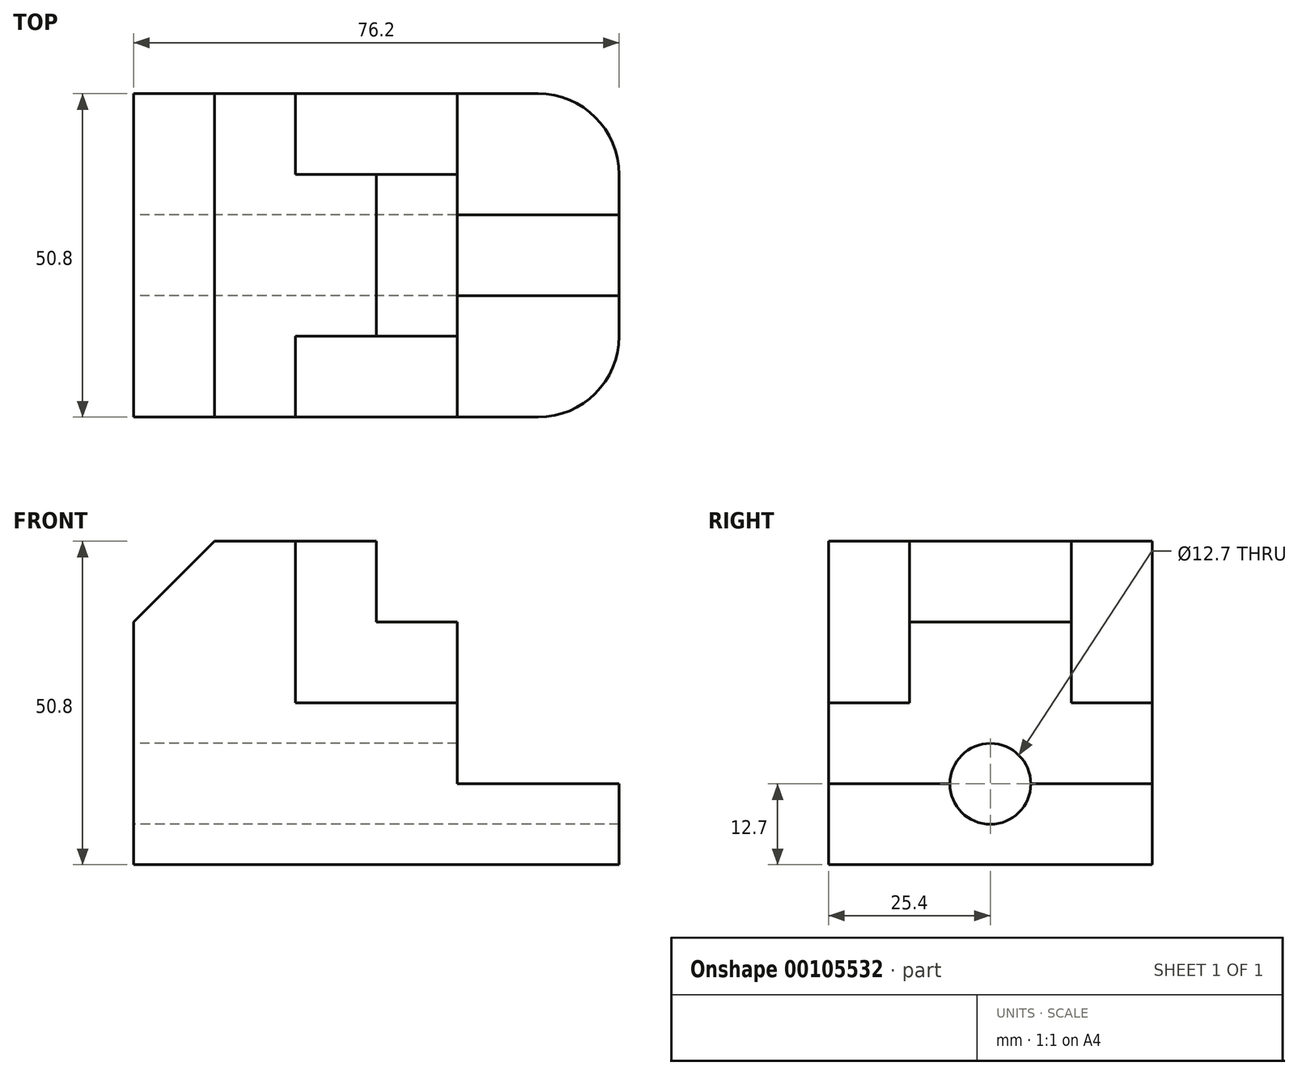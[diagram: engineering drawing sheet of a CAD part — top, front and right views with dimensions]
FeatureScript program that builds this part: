
annotation { "Feature Type Name" : "Feature", "Feature Type Description" : "" }
export const myFeature = defineFeature(function(context is Context, id is Id, definition is map)
    precondition{}
    {
        {
            var Q0;
            Q0=qCreatedBy(makeId("Front.planeOp"),FACE);
            var sketch = newSketch(context, id + "F0", { "sketchPlane" : qUnion([Q0])});
            skLineSegment(sketch, "E0", {"start": v(0, 0) * mm, "end": v(76.2, 0) * mm});
            skLineSegment(sketch, "E1", {"start": v(76.2, 0) * mm, "end": v(76.2, 12.7) * mm});
            skLineSegment(sketch, "E2", {"start": v(76.2, 12.7) * mm, "end": v(50.8, 12.7) * mm});
            skLineSegment(sketch, "E3", {"start": v(50.8, 12.7) * mm, "end": v(50.8, 25.4) * mm});
            skLineSegment(sketch, "E4", {"start": v(50.8, 25.4) * mm, "end": v(25.4, 25.4) * mm});
            skLineSegment(sketch, "E5", {"start": v(25.4, 25.4) * mm, "end": v(25.4, 50.8) * mm});
            skLineSegment(sketch, "E6", {"start": v(25.4, 50.8) * mm, "end": v(12.7, 50.8) * mm});
            skLineSegment(sketch, "E7", {"start": v(12.7, 50.8) * mm, "end": v(0, 38.1) * mm});
            skLineSegment(sketch, "E8", {"start": v(0, 38.1) * mm, "end": v(0, 0) * mm});
            skSolve(sketch);
        }
        {
            var Q0;
            Q0 = qSketchRegion(id + "F0", true);
            extrude(context, id + "F1", {"entities" : qUnion([Q0]), "endBound" : BoundingType.SYMMETRIC, "depth" : 50.8 * mm});
        }
        {
            var Q0;
            Q0=qCreatedBy(makeId("Front.planeOp"),FACE);
            var sketch = newSketch(context, id + "F2", { "sketchPlane" : qUnion([Q0])});
            skLineSegment(sketch, "E9", {"start": v(0, 0) * mm, "end": v(25.4, 0) * mm, "construction": true});
            skLineSegment(sketch, "E10", {"start": v(25.4, 0) * mm, "end": v(25.4, 25.4) * mm, "construction": true});
            skLineSegment(sketch, "E11", {"start": v(25.4, 25.4) * mm, "end": v(50.8, 25.4) * mm});
            skLineSegment(sketch, "E12", {"start": v(50.8, 25.4) * mm, "end": v(50.8, 38.1) * mm});
            skLineSegment(sketch, "E13", {"start": v(50.8, 38.1) * mm, "end": v(38.1, 38.1) * mm});
            skLineSegment(sketch, "E14", {"start": v(38.1, 38.1) * mm, "end": v(38.1, 50.8) * mm});
            skLineSegment(sketch, "E15", {"start": v(38.1, 50.8) * mm, "end": v(25.4, 50.8) * mm});
            skLineSegment(sketch, "E16", {"start": v(25.4, 50.8) * mm, "end": v(25.4, 25.4) * mm});
            skSolve(sketch);
        }
        {
            var Q0;
            Q0 = qSketchRegion(id + "F2", true);
            extrude(context, id + "F3", {"entities" : qUnion([Q0]), "operationType" : NewBodyOperationType.ADD, "endBound" : BoundingType.SYMMETRIC, "depth" : 25.4 * mm});
        }
        {
            var Q0;
            Q0=qCreatedBy(makeId("Top.planeOp"),FACE);
            var sketch = newSketch(context, id + "F4", { "sketchPlane" : qUnion([Q0])});
            skLineSegment(sketch, "E17", {"start": v(0, 0) * mm, "end": v(0, 25.4) * mm, "construction": true});
            skLineSegment(sketch, "E18", {"start": v(0, 25.4) * mm, "end": v(63.5, 25.4) * mm, "construction": true});
            skLineSegment(sketch, "E19", {"start": v(63.5, 25.4) * mm, "end": v(63.5, 12.7) * mm, "construction": true});
            skLineSegment(sketch, "E20", {"start": v(63.5, 12.7) * mm, "end": v(76.2, 12.7) * mm, "construction": true});
            skLineSegment(sketch, "E21", {"start": v(76.2, 12.7) * mm, "end": v(76.2, -12.7) * mm, "construction": true});
            skLineSegment(sketch, "E22", {"start": v(76.2, -12.7) * mm, "end": v(63.5, -12.7) * mm, "construction": true});
            skLineSegment(sketch, "E23", {"start": v(63.5, -12.7) * mm, "end": v(63.5, -25.4) * mm, "construction": true});
            skLineSegment(sketch, "E24", {"start": v(63.5, -25.4) * mm, "end": v(0, -25.4) * mm, "construction": true});
            skLineSegment(sketch, "E25", {"start": v(0, -25.4) * mm, "end": v(0, 0) * mm, "construction": true});
            skLineSegment(sketch, "E26", {"start": v(0, -25.4) * mm, "end": v(0, 25.4) * mm});
            skLineSegment(sketch, "E27", {"start": v(76.2, 12.7) * mm, "end": v(76.2, -12.7) * mm});
            skLineSegment(sketch, "E28", {"start": v(63.5, -25.4) * mm, "end": v(0, -25.4) * mm});
            skArc(sketch, "E29", {"start": v(76.2, 12.7) * mm, "mid": v(72.48, 21.68) * mm, "end": v(63.5, 25.4) * mm});
            skArc(sketch, "E30", {"start": v(63.5, -25.4) * mm, "mid": v(72.48, -21.68) * mm, "end": v(76.2, -12.7) * mm});
            skLineSegment(sketch, "E31", {"start": v(63.5, 25.4) * mm, "end": v(0, 25.4) * mm});
            skSolve(sketch);
        }
        {
            var Q0;
            Q0 = qSketchRegion(id + "F4", true);
            extrude(context, id + "F5", {"entities" : qUnion([Q0]), "operationType" : NewBodyOperationType.INTERSECT, "depth" : 76.2 * mm});
        }
        {
            var Q0;
            Q0=qCreatedBy(makeId("Right.planeOp"),FACE);
            var sketch = newSketch(context, id + "F6", { "sketchPlane" : qUnion([Q0])});
            skCircle(sketch, "E32", {"center": v(0, 12.7) * mm, "radius": 6.35 * mm});
            skSolve(sketch);
        }
        {
            var Q0;
            Q0 = qSketchRegion(id + "F6", true);
            extrude(context, id + "F7", {"entities" : qUnion([Q0]), "operationType" : NewBodyOperationType.REMOVE, "depth" : 76.2 * mm});
        }
    });
